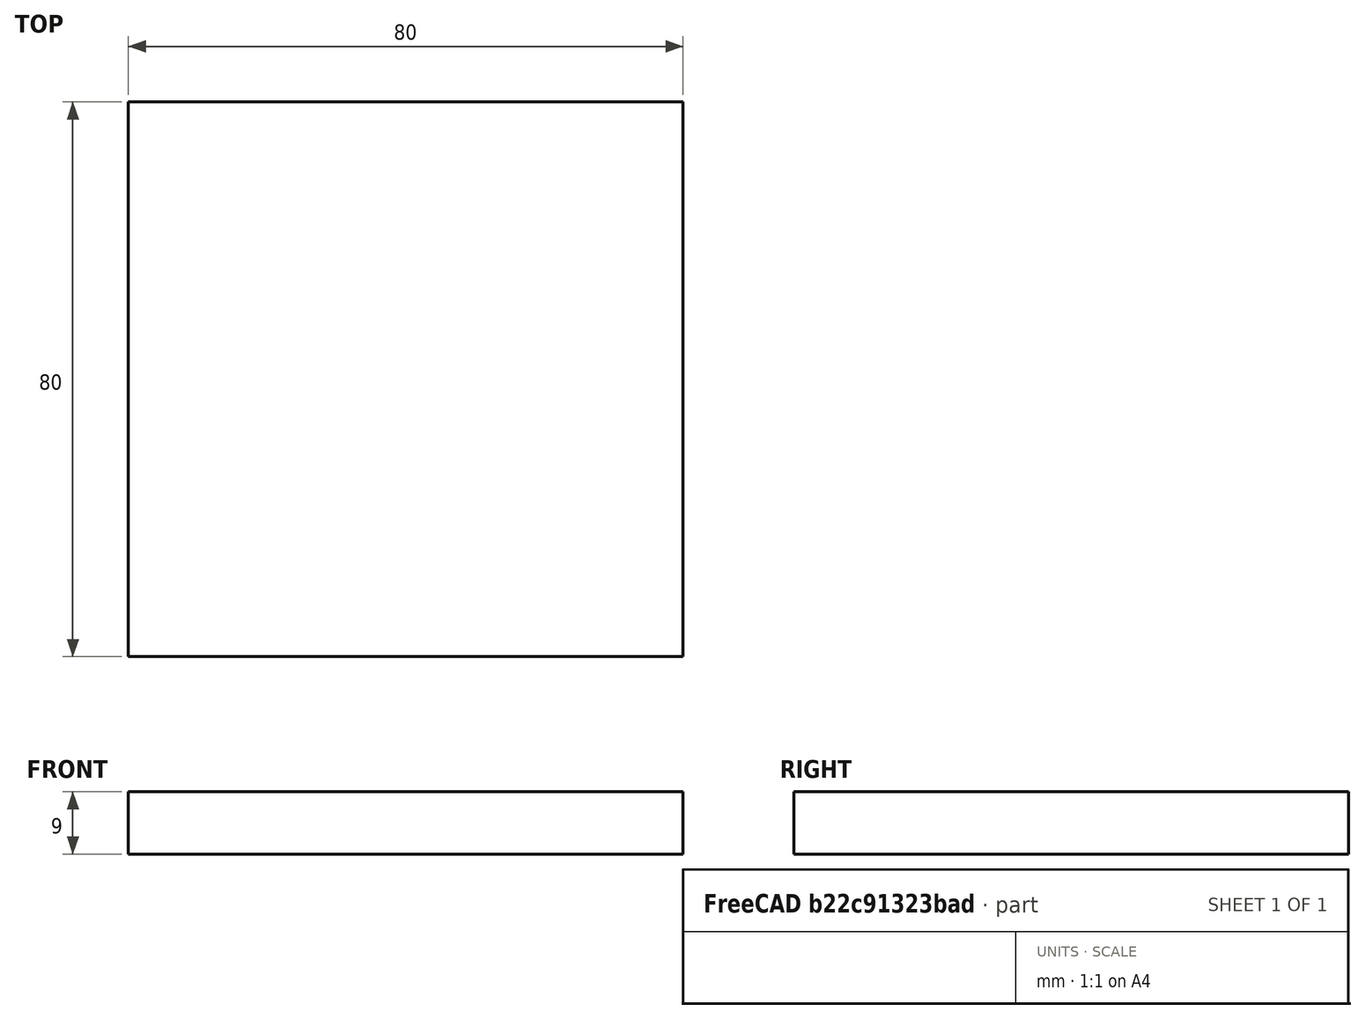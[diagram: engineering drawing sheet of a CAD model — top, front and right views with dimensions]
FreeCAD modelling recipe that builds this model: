
FCSTD DOCUMENT  (FreeCAD 0.16RUnknown)
Label: balise_haut
License: All rights reserved
LicenseURL: http://en.wikipedia.org/wiki/All_rights_reserved
objects: App::FeaturePython×2, Drawing::FeatureViewPart×2, Part::Plane×1, Part::FeaturePython×1, Part::Extrusion×1, App::DocumentObjectGroup×1, Drawing::FeatureViewPython×1, Drawing::FeaturePage×1
note: 3 computed .brp shape members not serialized (recipe doc carries the construction recipe); baked Part::Feature solids carry a one-line shape summary decoded from their .brp

FEATURE [Part::Plane] square
  Length = 80
  Placement = pos=(0,-40,0) rot=(0,0,1;0rad)
  Width = 80
FEATURE [Part::FeaturePython] RefineLinearExtrude  # WARN: FeaturePython — macro-defined, semantics opaque (R4)
  Base = -> square
FEATURE [Part::Extrusion] LinearExtrude
  Base = -> RefineLinearExtrude
  Dir = (0,0,9)
  Solid = true
FEATURE [App::FeaturePython] Dimension  # Draft dimension (typed FeaturePython)
  Dimline = (0,46,0)
  Direction = (0,0,0)
  Distance = 80
  End = (80,40,0)
  Normal = (0,0,1)
  Start = (0,40,0)
FEATURE [App::FeaturePython] Dimension001  # Draft dimension (typed FeaturePython)
  Dimline = (86,0,0)
  Direction = (0,0,0)
  Distance = 80
  End = (80,-40,0)
  Normal = (0,0,1)
  Start = (80,40,0)
FEATURE [App::DocumentObjectGroup] Groupe  label="Dimensions XY"
  Group = -> [Dimension,Dimension001]
FEATURE [Drawing::FeatureViewPython] ViewGroupe  # drawing view (typed FeaturePython)
  Direction = (0,0,0)
  FillStyle = 0
  FontSize = 12
  LineStyle = 0
  LineWidth = 0.35
  Rotation = -90
  Scale = 1.5
  Source = -> Groupe
  ViewResult = <g id="ViewGroupe" transform="rotate(-90.0,123.33,199.17) translate(123.33,199.17) scale(1.5,-1.5)"><path d="M 0.0 40.0 L 0.0 46.0 L 80.0 46.0 L 80.0 40.0" fill="none" stroke="#000000" stroke-width="0.233333333333 px" style="stroke-width:0.233333333333;stroke-miterlimit:4;stroke-dasharray:none" freecad:basepoint1="0.0 40.0" freecad:basepoint2="80.0 40.0" freecad:dimpoint="0.0 46.0"/>\n<path transform="rotate(-0.0,0.0,46.0) translate(0.0,46.0) scale(0.666666666667,0.666666666667)" freecad:skip="1" fill="#000000" stroke="none" style="stroke-miterlimit:4;stroke-dasharray:none" d="M 0 0 L 4 1 L 4 -1 Z"/>\n<path transform="rotate(180.0,80.0,46.0) translate(80.0,46.0) scale(0.666666666667,0.666666666667)" freecad:skip="1" fill="#000000" stroke="none" style="stroke-miterlimit:4;stroke-dasharray:none" d="M 0 0 L 4 1 L 4 -1 Z"/>\n<text fill="#000000" font-size="4.0" style="text-anchor:middle;text-align:center;font-family:" transform="rotate(-0.0,40.0,47.0) translate(40.0,47.0) scale(1,-1) " freecad:skip="1">\n80,00 </text>\n<path d="M 80.0 40.0 L 86.0 40.0 L 86.0 -40.0 L 80.0 -40.0" fill="none" stroke="#000000" stroke-width="0.233333333333 px" style="stroke-width:0.233333333333;stroke-miterlimit:4;stroke-dasharray:none" freecad:basepoint1="80.0 40.0" freecad:basepoint2="80.0 -40.0" freecad:dimpoint="86.0 40.0"/>\n<path transform="rotate(-90.0,86.0,40.0) translate(86.0,40.0) scale(0.666666666667,0.666666666667)" freecad:skip="1" fill="#000000" stroke="none" style="stroke-miterlimit:4;stroke-dasharray:none" d="M 0 0 L 4 1 L 4 -1 Z"/>\n<path transform="rotate(90.0,86.0,-40.0) translate(86.0,-40.0) scale(0.666666666667,0.666666666667)" freecad:skip="1" fill="#000000" stroke="none" style="stroke-miterlimit:4;stroke-dasharray:none" d="M 0 0 L 4 1 L 4 -1 Z"/>\n<text fill="#000000" font-size="4.0" style="text-anchor:middle;text-align:center;font-family:" transform="rotate(-90.0,87.0,0.0) translate(87.0,0.0) scale(1,-1) " freecad:skip="1">\n80,00 </text>\n</g>
  Visible = true
  X = 123.33
  Y = 199.17
FEATURE [Drawing::FeatureViewPart] Ortho001  label="Ortho_0_-1"
  Direction = (0,0,1)
  HiddenWidth = 0.15
  LineWidth = 0.35
  Rotation = 90
  Scale = 1.5
  ShowHiddenLines = false
  ShowSmoothLines = false
  Source = -> LinearExtrude
  Tolerance = 0.05
  ViewResult = <g id="Ortho_0_-1"\n   transform="rotate(90,123.33,79.17) translate(123.33,79.17) scale(1.5,1.5)"\n  >\n<g   stroke="rgb(0, 0, 0)"\n   stroke-width="0.233333"\n   stroke-linecap="butt"\n   stroke-linejoin="miter"\n   fill="none"\n   transform="scale(1,-1)"\n  >\n<path id= "1" d=" M 0 -40 L 0 40 " />\n<path id= "2" d=" M 0 -40 L 80 -40 " />\n<path id= "3" d=" M 80 -40 L 80 40 " />\n<path id= "4" d=" M 0 40 L 80 40 " />\n</g>\n</g>
  Visible = true
  X = 123.33
  Y = 79.17
FEATURE [Drawing::FeatureViewPart] Ortho002  label="Ortho_1_-1"
  Direction = (0.57735,-0.57735,0.57735)
  HiddenWidth = 0.15
  LineWidth = 0.35
  Rotation = 60
  Scale = 1.5
  ShowHiddenLines = false
  ShowSmoothLines = false
  Source = -> LinearExtrude
  Tolerance = 0.05
  ViewResult = <g id="Ortho_1_-1"\n   transform="rotate(60,254.24,120.183) translate(254.24,120.183) scale(1.5,1.5)"\n  >\n<g   stroke="rgb(0, 0, 0)"\n   stroke-width="0.233333"\n   stroke-linecap="butt"\n   stroke-linejoin="miter"\n   fill="none"\n   transform="scale(1,-1)"\n  >\n<path id= "1" d=" M 0 -32.6599 L -6.36396 -28.9856 " />\n<path id= "2" d=" M -6.36396 -28.9856 L -6.36396 36.3341 " />\n<path id= "3" d=" M 56.5685 0 L 50.2046 3.67423 " />\n<path id= "4" d=" M 0 -32.6599 L 56.5685 0 " />\n<path id= "5" d=" M -6.36396 -28.9856 L 50.2046 3.67423 " />\n<path id= "6" d=" M 56.5685 65.3197 L 50.2046 68.994 " />\n<path id= "7" d=" M 56.5685 0 L 56.5685 65.3197 " />\n<path id= "8" d=" M 50.2046 3.67423 L 50.2046 68.994 " />\n<path id= "9" d=" M -6.36396 36.3341 L 50.2046 68.994 " />\n</g>\n</g>
  Visible = true
  X = 254.24
  Y = 120.183
FEATURE [Drawing::FeaturePage] Page
  EditableTexts = AUTHOR NAME | CREATION DATE | SUPERVISOR NAME | CHECK DATE | 1,5 | WEIGHT | NUMBER | SHEET | Balise | Haut
  Group = -> [ViewGroupe,Ortho001,Ortho002]
